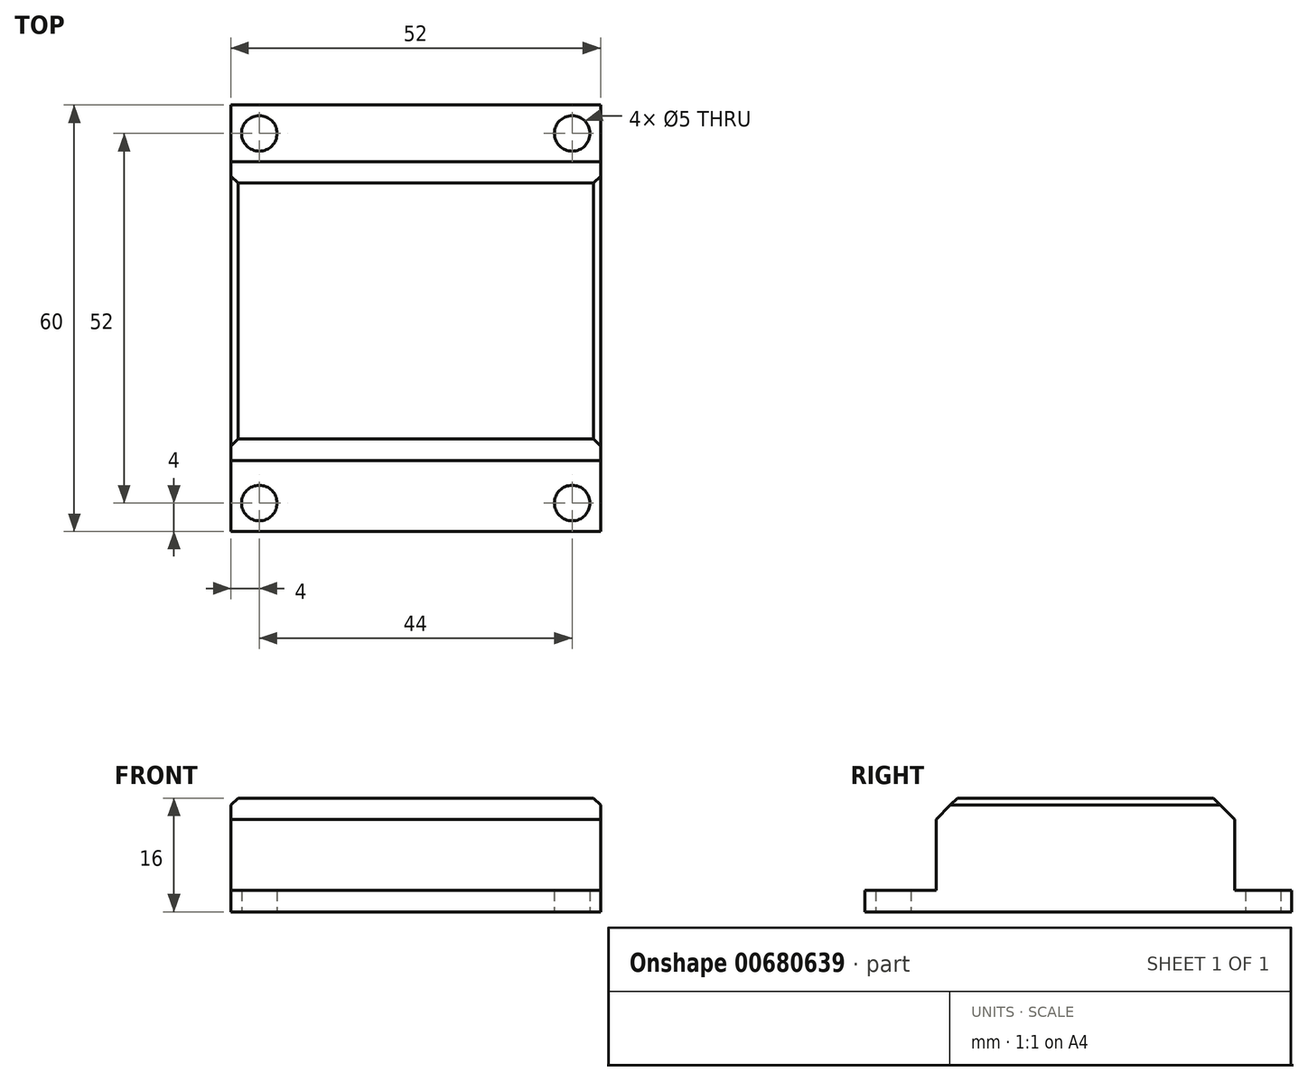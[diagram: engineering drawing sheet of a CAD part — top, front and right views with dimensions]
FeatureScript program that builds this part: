
annotation { "Feature Type Name" : "Feature", "Feature Type Description" : "" }
export const myFeature = defineFeature(function(context is Context, id is Id, definition is map)
    precondition{}
    {
        {
            var Q0;
            Q0=qCreatedBy(makeId("Top.planeOp"),FACE);
            var sketch = newSketch(context, id + "F0", { "sketchPlane" : qUnion([Q0])});
            skLineSegment(sketch, "E0.bottom", {"start": v(-26, 30) * mm, "end": v(26, 30) * mm});
            skLineSegment(sketch, "E0.top", {"start": v(-26, -30) * mm, "end": v(26, -30) * mm});
            skLineSegment(sketch, "E0.left", {"start": v(-26, 30) * mm, "end": v(-26, -30) * mm});
            skLineSegment(sketch, "E0.right", {"start": v(26, 30) * mm, "end": v(26, -30) * mm});
            skCircle(sketch, "E1", {"center": v(-22, 26) * mm, "radius": 2.5 * mm});
            skLineSegment(sketch, "E2.MirrorCS", {"start": v(-26, 90) * mm, "end": v(26, 90) * mm});
            skCircle(sketch, "E3.MirrorC", {"center": v(22, 26) * mm, "radius": 2.5 * mm});
            skCircle(sketch, "E4.MirrorC", {"center": v(22, -26) * mm, "radius": 2.5 * mm});
            skCircle(sketch, "E5.MirrorC", {"center": v(-22, -26) * mm, "radius": 2.5 * mm});
            skSolve(sketch);
        }
        {
            var Q0;
            Q0 = qSketchRegion(id + "F0", true);
            extrude(context, id + "F1", {"entities" : qUnion([Q0]), "depth" : 3 * mm, "offsetDistance" : 25 * mm});
        }
        {
            var Q0;
            Q0=makeQuery(id+"F1.opExtrude","CAP_FACE",FACE,{"disambiguationData":[OSD([sQuery(id+"F0.wireOp",EDGE,"E0.bottom"),sQuery(id+"F0.wireOp",EDGE,"E0.top"),sQuery(id+"F0.wireOp",EDGE,"E0.left"),sQuery(id+"F0.wireOp",EDGE,"E0.right")])],"isStart":false});
            var sketch = newSketch(context, id + "F2", { "sketchPlane" : qUnion([Q0])});
            skLineSegment(sketch, "E6.bottom", {"start": v(-26, 22) * mm, "end": v(26, 22) * mm});
            skLineSegment(sketch, "E6.top", {"start": v(-26, -20) * mm, "end": v(26, -20) * mm});
            skLineSegment(sketch, "E6.left", {"start": v(-26, 22) * mm, "end": v(-26, -20) * mm});
            skLineSegment(sketch, "E6.right", {"start": v(26, 22) * mm, "end": v(26, -20) * mm});
            skSolve(sketch);
        }
        {
            var Q0;
            Q0 = qSketchRegion(id + "F2", true);
            extrude(context, id + "F3", {"entities" : qUnion([Q0]), "operationType" : NewBodyOperationType.ADD, "depth" : 13 * mm, "offsetDistance" : 25 * mm});
        }
        {
            var Q0;
            Q0=makeQuery(id+"F3.opExtrude","CAP_EDGE",EDGE,{"disambiguationData":[OSD([sQuery(id+"F2.wireOp",EDGE,"E6.top")])],"isStart":false});
            chamfer(context, id + "F4", {"entities" : qUnion([Q0]), "width" : 3 * mm, "tangentPropagation" : true});
        }
        {
            var Q0;
            Q0=makeQuery(id+"F3.opExtrude","CAP_EDGE",EDGE,{"disambiguationData":[OSD([sQuery(id+"F2.wireOp",EDGE,"E6.bottom")])],"isStart":false});
            chamfer(context, id + "F5", {"entities" : qUnion([Q0]), "width" : 3 * mm, "tangentPropagation" : true});
        }
        {
            var Q0;
            Q0=makeQuery(id+"F3.opExtrude","CAP_EDGE",EDGE,{"disambiguationData":[OSD([sQuery(id+"F2.wireOp",EDGE,"E6.left")])],"isStart":false});
            chamfer(context, id + "F6", {"entities" : qUnion([Q0]), "width" : 1 * mm, "tangentPropagation" : true});
        }
        {
            var Q0;
            Q0=makeQuery(id+"F3.opExtrude","CAP_EDGE",EDGE,{"disambiguationData":[OSD([sQuery(id+"F2.wireOp",EDGE,"E6.right")])],"isStart":false});
            chamfer(context, id + "F7", {"entities" : qUnion([Q0]), "width" : 1 * mm, "tangentPropagation" : true});
        }
    });
